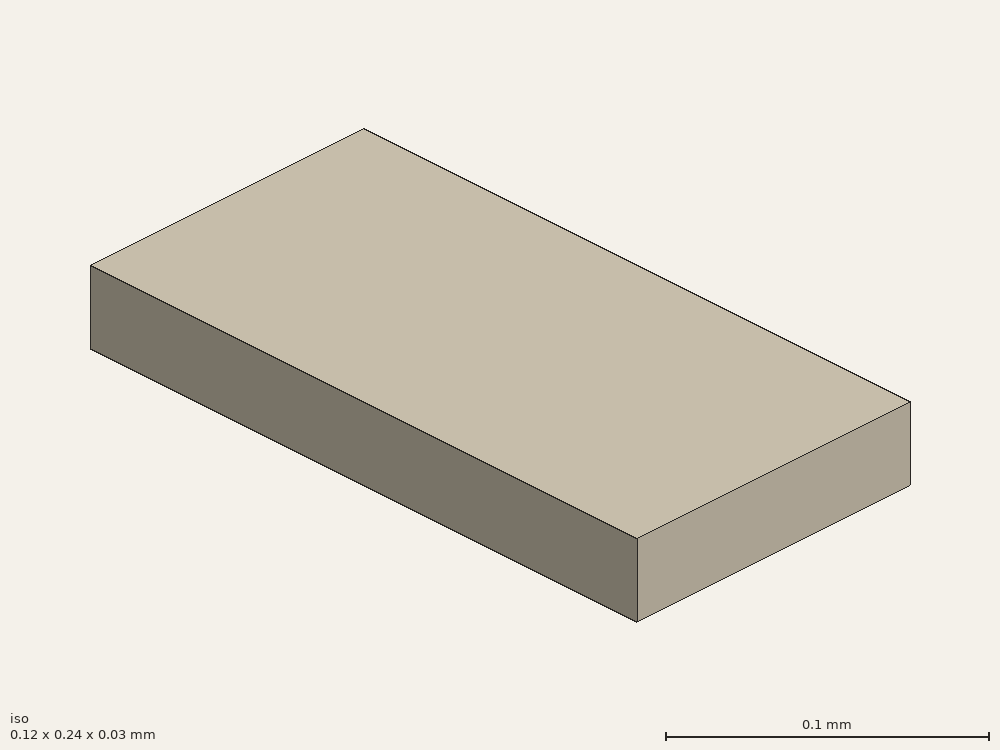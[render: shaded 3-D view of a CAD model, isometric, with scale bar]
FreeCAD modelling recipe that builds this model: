
FCSTD DOCUMENT  (FreeCAD 0.15R4671 (Git))
Label: quadrangle1
License: All rights reserved
LicenseURL: http://en.wikipedia.org/wiki/All_rights_reserved
objects: Sketcher::SketchObject×1, PartDesign::Pad×1
note: 3 computed .brp shape members not serialized (recipe doc carries the construction recipe); baked Part::Feature solids carry a one-line shape summary decoded from their .brp

FEATURE [Sketcher::SketchObject] Sketch
  sketch-geometry (4):
    g0: LineSegment StartX=0.06 StartY=0.12 StartZ=0 EndX=-0.06 EndY=0.12 EndZ=0
    g1: LineSegment StartX=-0.06 StartY=0.12 StartZ=0 EndX=-0.06 EndY=-0.12 EndZ=0
    g2: LineSegment StartX=-0.06 StartY=-0.12 StartZ=0 EndX=0.06 EndY=-0.12 EndZ=0
    g3: LineSegment StartX=0.06 StartY=-0.12 StartZ=0 EndX=0.06 EndY=0.12 EndZ=0
  constraints (13):
    c: Coincident(g0,g1)
    c: Coincident(g1,g2)
    c: Coincident(g2,g3)
    c: Coincident(g3,g0)
    c: Horizontal(g0)
    c: Horizontal(g2)
    c: Vertical(g1)
    c: Vertical(g3)
    c: Symmetric(g0,g2,g-1)
    c: Equal(g0,g2)
    c: Equal(g3,g1)
    c: DistanceY(g0,g1) = -0.24
    c: DistanceX(g0,g0) = 0.12
FEATURE [PartDesign::Pad] Pad
  Length = 0.03
  Length2 = 100
  Midplane = true
  Sketch = -> Sketch
  Type = 0
